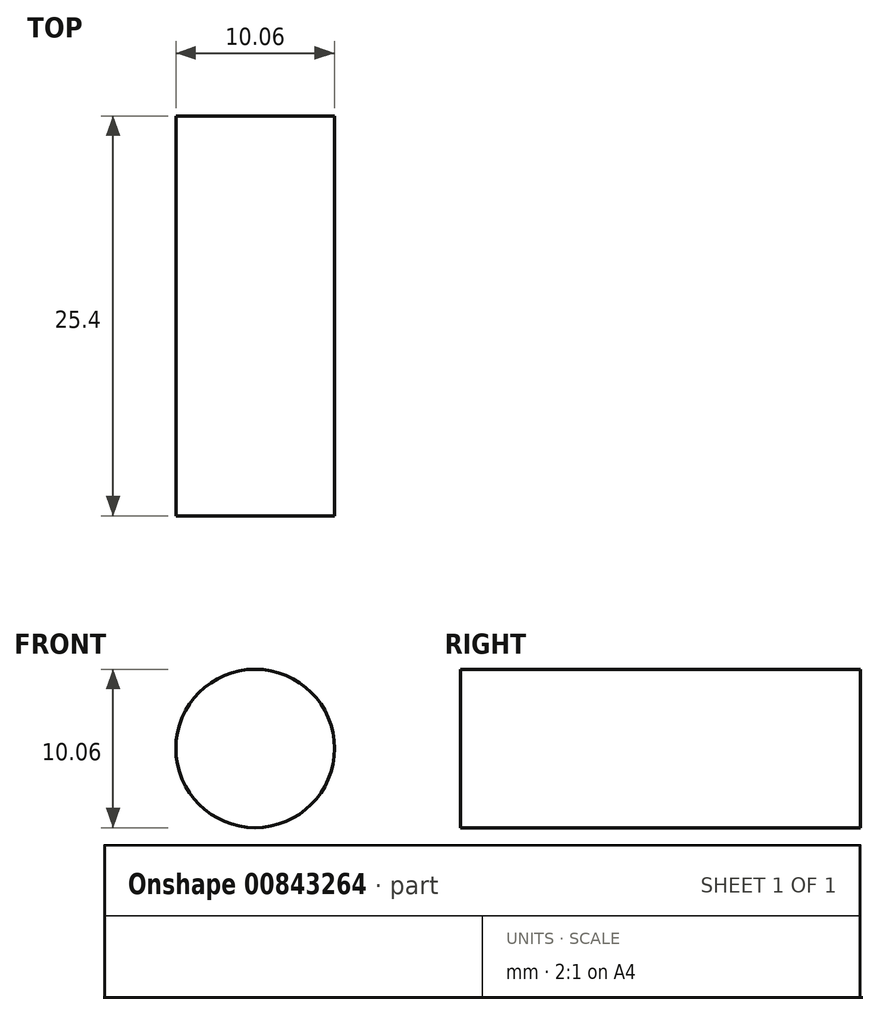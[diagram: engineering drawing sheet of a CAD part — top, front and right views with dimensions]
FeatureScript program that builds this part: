
annotation { "Feature Type Name" : "Feature", "Feature Type Description" : "" }
export const myFeature = defineFeature(function(context is Context, id is Id, definition is map)
    precondition{}
    {
        {
            var Q0;
            Q0=qCreatedBy(makeId("Front.planeOp"),FACE);
            var sketch = newSketch(context, id + "F0", { "sketchPlane" : qUnion([Q0])});
            skCircle(sketch, "E0", {"center": v(0, 0) * mm, "radius": 5.03 * mm});
            skSolve(sketch);
        }
        {
            var Q0;
            Q0=makeQuery(id+"F0.imprint","IMPRINT",FACE,{"disambiguationData":[TD([[makeQuery(id+"F0.imprint","IMPRINT",EDGE,{"derivedFrom":sQuery(id+"F0.wireOp",EDGE,"E0")}),1.0]])]});
            extrude(context, id + "F1", {"entities" : qUnion([Q0]), "depth" : 25.4 * mm, "offsetDistance" : 25.4 * mm});
        }
    });
